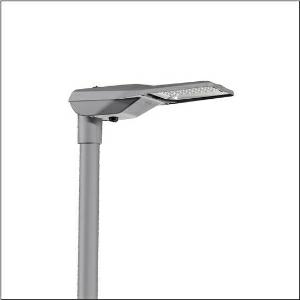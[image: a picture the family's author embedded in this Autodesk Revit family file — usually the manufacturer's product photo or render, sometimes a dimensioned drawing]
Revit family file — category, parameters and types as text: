
# Revit family: streetlight_sl_21_iq_mini___p0_8ab_5xe2r31y08jb_bd99
name_source: partatom
category: Lighting Fixtures
units: mm (PartAtom-declared; Revit-internal decimal feet)

## family parameters
Cut with Voids When Loaded = No
Host = Face
Light Source = No
Part Type = Normal
Room Calculation Point = No
Round Connector Dimension = Use Diameter
Shared = No

## types (1)
- --- (1 x LED, 9740 lm, 72.5 W, 3000K)
    Apparent Load = 73 VA
    CIE Flux Codes = 39 72 97 100 100
    Color Rendering = 70
    Color Temperature = 3000K
    Default Elevation = 1800 mm
    Description = Streetlight SL 21 iQ mini, mast luminaire, primary light control with lens, of PMMA, primary optical cover: cover, of toughened safety glass, transparent, light distribution: P0.8aB, light emission: direct distribution, primary light characteristic: asymmetric, installation type: post-top, side-entry, LED, High Power LED, rated luminous flux: 9.740lm, luminous efficacy: 134lm/W, light colour: 730, colour temperature: 3000K, control gear: iQ-Street Remote, D4i with power reduction, control: pre-setting: logarithmic dimming characteristic, Street-Remote, Auto-Match, Temp-Guard, Lumen-Switch, Night-Set, Smart-Wire, Light-Fading, Desk-Remote (wireless, voltage-free reading and setting of iQ features in the workshop via application-optimized NFC function/RFID function), optimised constant luminous flux control (CLO 2.0), mains connection: 220..240V, AC, 50/60Hz, start of lifetime: 73W, end of service life: 76W, reduction: 33W, luminaire housing, of diecast aluminium, powder-coated, SITECO metallic grey (DB 702S), corrosivity category C5 high according to DIN EN ISO 12944, please order mast flange separately, inclination adjustable: 0°, 5°, 10°, 15°, sealing non-destructively replaceable, multi-level sealing system, length: 628mm, width: 235mm, height: 110mm, mast flange for spigot size: 42mm (side-entry): 5XC10008XM4, 60/48mm (side-entry/post-top): 5XC10108XM2, 76/60mm (side-entry/post-top): 5XC10108XM1, mounting height: 4..8m, Smart Interface below and above, protection rating (complete): IP66, insulation class (complete): insulation class II (safety insulation), certification: CE, ENEC, ENEC+, VDE, impact resistance: IK10, permissible operating ambient temperature for outdoor applications: -40..+50°C, standard-compliant lighting for roads and squares, packaging unit: 1 piece

Light Distribution: P0.8aB
    Height = 110 mm
    Lamp = 1 x LED
    Lamp Light Flux = 9740 lm
    Lamp Power = 72.5 W
    Lamp count = 1
    Length = 625 mm
    Luminous efficacy = 134 lm/W
    Manufacturer = Siteco
    ModVariant = No
    Model = 5XE2R31Y08JB
    Number of Poles = 1
    OnlyDefault = Yes
    Power Factor = 1
    Product Name = Streetlight SL 21 iQ mini | P0.8aB
    Product group = mast luminaire | pylon top
    ProductGroupID = 6100
    Protection Class = Protection class II
    Protection Degree = IP 66
    RLX_Detail_Level = 1
    RLX_Emergency_Light_Flux = 0 lm
    RLX_Emergency_Type = 0
    RLX_Emergency_Type_DB = No
    RlxData = <blob elided: 92109 chars, md5=0437cadd>
    Socket = socket
    Standby Power = 0 W
    System Light Flux = 9740 lm
    System Power = 73 W
    Type Comments = factory setting: luminous flux: 100 % | dim-lin: 254 | 755 mA
    Type Image = l_1003514.jpg
    URL = http://relux.com
    VarID = @adj_079029
    Voltage = 0 V
    Weight = 0.00 kg
    Width = 234 mm

## geometry (parser evidence)
native form markers: Blend x4, Sweep x11
no freeform markers — native parametric forms only
